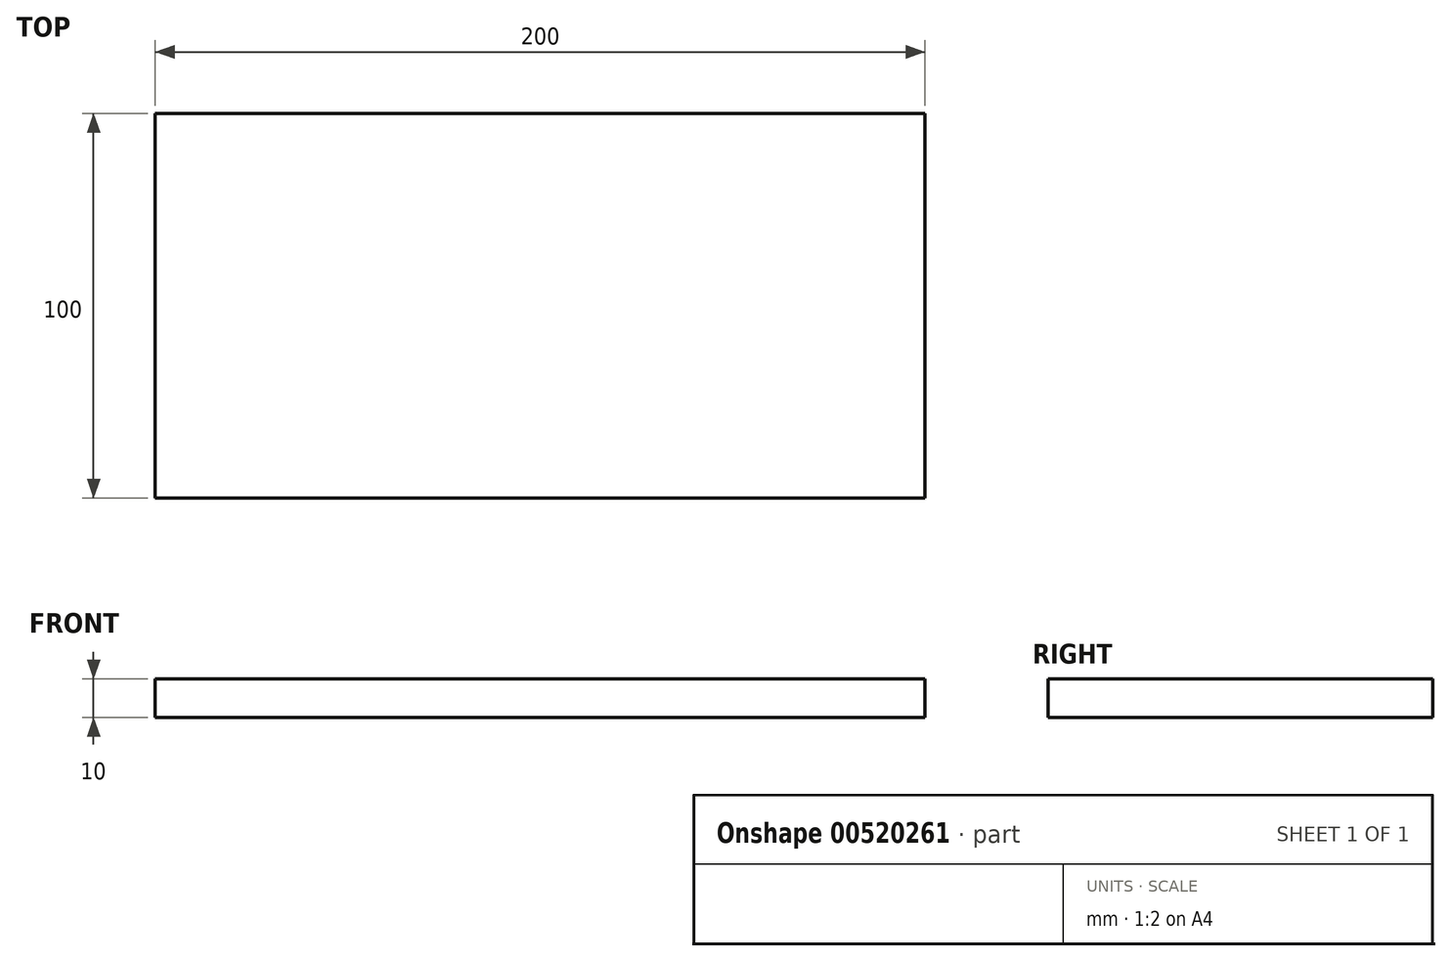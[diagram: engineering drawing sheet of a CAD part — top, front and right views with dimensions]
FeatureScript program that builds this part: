
annotation { "Feature Type Name" : "Feature", "Feature Type Description" : "" }
export const myFeature = defineFeature(function(context is Context, id is Id, definition is map)
    precondition{}
    {
        {
            var Q0;
            Q0=qCreatedBy(makeId("Top.planeOp"),FACE);
            var sketch = newSketch(context, id + "F0", { "sketchPlane" : qUnion([Q0])});
            skLineSegment(sketch, "E0.bottom", {"start": v(-83.13, 50.5) * mm, "end": v(116.87, 50.5) * mm});
            skLineSegment(sketch, "E0.top", {"start": v(-83.13, -49.5) * mm, "end": v(116.87, -49.5) * mm});
            skLineSegment(sketch, "E0.left", {"start": v(-83.13, 50.5) * mm, "end": v(-83.13, -49.5) * mm});
            skLineSegment(sketch, "E0.right", {"start": v(116.87, 50.5) * mm, "end": v(116.87, -49.5) * mm});
            skSolve(sketch);
        }
        {
            var Q0;
            Q0=makeQuery(id+"F0.imprint","IMPRINT",FACE,{"disambiguationData":[TD([[makeQuery(id+"F0.imprint","IMPRINT",EDGE,{"derivedFrom":sQuery(id+"F0.wireOp",EDGE,"E0.bottom")}),-1.0]])]});
            extrude(context, id + "F1", {"entities" : qUnion([Q0]), "depth" : 10 * mm, "offsetDistance" : 25 * mm});
        }
    });
